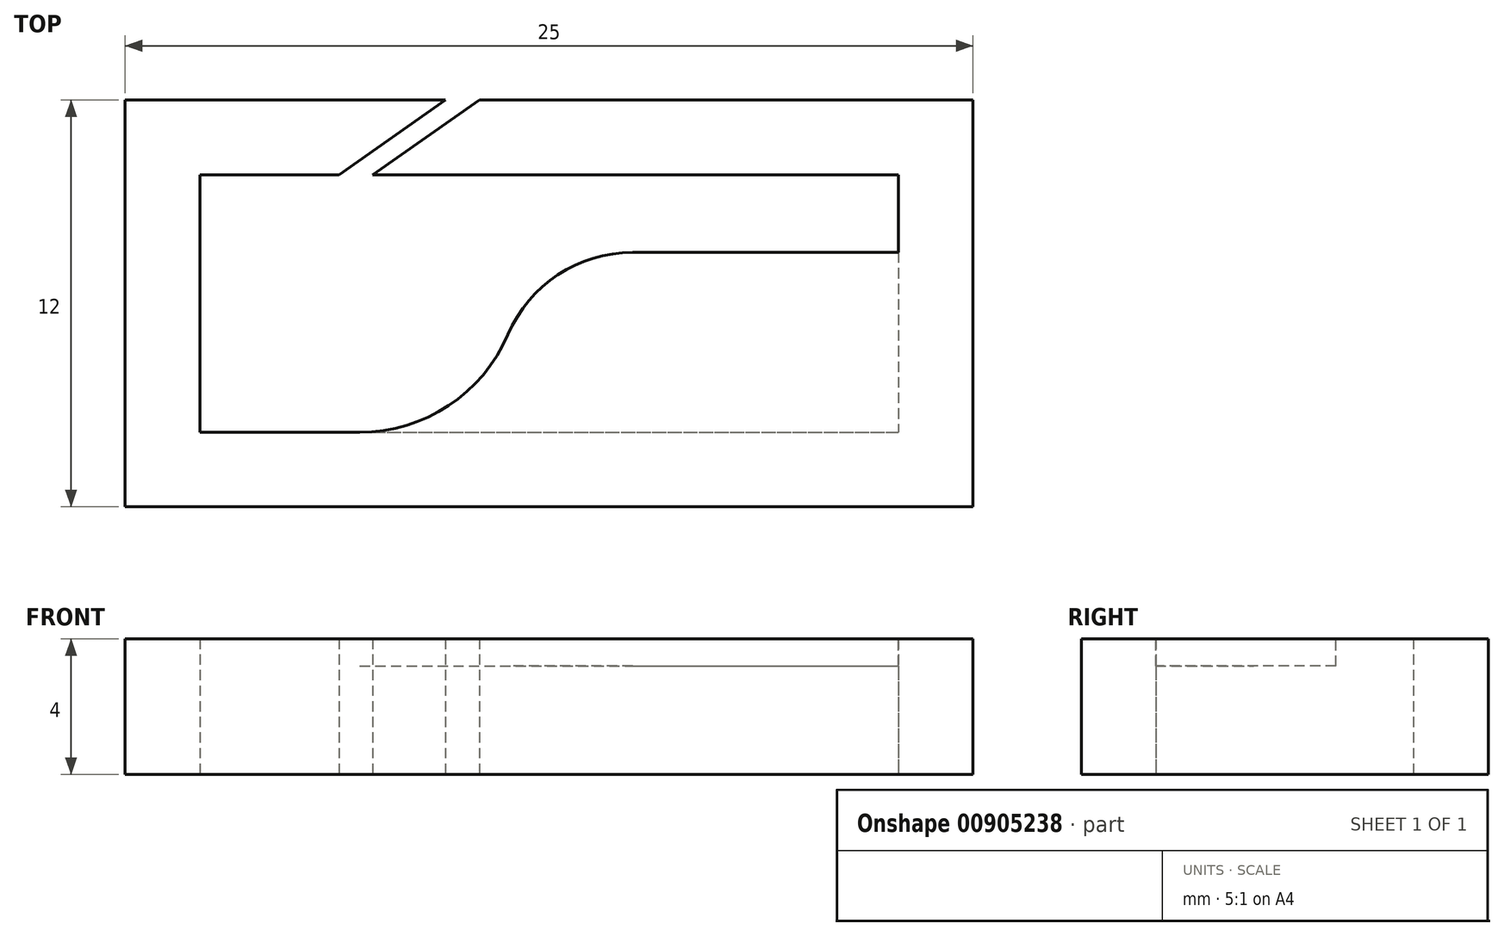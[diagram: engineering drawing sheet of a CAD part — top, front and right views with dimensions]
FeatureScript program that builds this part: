
annotation { "Feature Type Name" : "Feature", "Feature Type Description" : "" }
export const myFeature = defineFeature(function(context is Context, id is Id, definition is map)
    precondition{}
    {
        {
            var Q0;
            Q0=qCreatedBy(makeId("Top.planeOp"),FACE);
            var sketch = newSketch(context, id + "F0", { "sketchPlane" : qUnion([Q0])});
            skLineSegment(sketch, "E0.bottom", {"start": v(-18.57, -20.66) * mm, "end": v(-9.13, -20.66) * mm});
            skLineSegment(sketch, "E0.top", {"start": v(-18.57, -32.66) * mm, "end": v(6.43, -32.66) * mm});
            skLineSegment(sketch, "E0.left", {"start": v(-18.57, -20.66) * mm, "end": v(-18.57, -32.66) * mm});
            skLineSegment(sketch, "E0.right", {"start": v(6.43, -20.66) * mm, "end": v(6.43, -32.66) * mm});
            skLineSegment(sketch, "E1.0", {"start": v(-16.37, -22.86) * mm, "end": v(-16.37, -30.46) * mm});
            skLineSegment(sketch, "E1.1", {"start": v(-11.27, -22.86) * mm, "end": v(4.23, -22.86) * mm});
            skLineSegment(sketch, "E1.2", {"start": v(4.23, -22.86) * mm, "end": v(4.23, -30.46) * mm});
            skLineSegment(sketch, "E1.3", {"start": v(-16.37, -30.46) * mm, "end": v(4.23, -30.46) * mm});
            skLineSegment(sketch, "E2", {"start": v(-12.27, -22.86) * mm, "end": v(-9.13, -20.66) * mm});
            skLineSegment(sketch, "E3", {"start": v(-11.27, -22.86) * mm, "end": v(-8.13, -20.66) * mm});
            skLineSegment(sketch, "E4.trimOffspring", {"start": v(-8.13, -20.66) * mm, "end": v(6.43, -20.66) * mm});
            skLineSegment(sketch, "E5", {"start": v(-16.37, -22.86) * mm, "end": v(-12.27, -22.86) * mm});
            skSolve(sketch);
        }
        {
            var Q0;
            Q0=makeQuery(id+"F0.imprint","IMPRINT",FACE,{"disambiguationData":[TD([[makeQuery(id+"F0.imprint","IMPRINT",EDGE,{"derivedFrom":sQuery(id+"F0.wireOp",EDGE,"E0.bottom")}),-1.0]])]});
            extrude(context, id + "F1", {"entities" : qUnion([Q0]), "depth" : 4 * mm, "offsetDistance" : 25 * mm});
        }
        {
            var Q0;
            Q0=makeQuery(id+"F1.opExtrude","CAP_FACE",FACE,{"disambiguationData":[OSD([sQuery(id+"F0.wireOp",EDGE,"E0.bottom"),sQuery(id+"F0.wireOp",EDGE,"E0.top"),sQuery(id+"F0.wireOp",EDGE,"E0.left"),sQuery(id+"F0.wireOp",EDGE,"E0.right"),sQuery(id+"F0.wireOp",EDGE,"E1.0"),sQuery(id+"F0.wireOp",EDGE,"E1.1"),sQuery(id+"F0.wireOp",EDGE,"E1.2"),sQuery(id+"F0.wireOp",EDGE,"E1.3"),sQuery(id+"F0.wireOp",EDGE,"E2"),sQuery(id+"F0.wireOp",EDGE,"E3"),sQuery(id+"F0.wireOp",EDGE,"E4.trimOffspring"),sQuery(id+"F0.wireOp",EDGE,"E5")])],"isStart":false});
            var sketch = newSketch(context, id + "F2", { "sketchPlane" : qUnion([Q0])});
            skLineSegment(sketch, "E6.bottom", {"start": v(-11.65, -31.16) * mm, "end": v(6.43, -31.16) * mm});
            skLineSegment(sketch, "E6.top", {"start": v(-3.6, -25.16) * mm, "end": v(6.43, -25.16) * mm});
            skLineSegment(sketch, "E6.right", {"start": v(6.43, -31.16) * mm, "end": v(6.43, -25.16) * mm});
            skArc(sketch, "E7", {"start": v(-11.65, -30.46) * mm, "mid": v(-9.04, -29.68) * mm, "end": v(-7.28, -27.58) * mm});
            skPoint(sketch, "E8.visualSharp", {"position": v(-6.93, -25.16) * mm});
            skArc(sketch, "E8.filletArc", {"start": v(-3.6, -25.16) * mm, "mid": v(-5.8, -25.82) * mm, "end": v(-7.28, -27.58) * mm});
            skLineSegment(sketch, "E9", {"start": v(-11.65, -30.46) * mm, "end": v(-11.65, -31.16) * mm});
            skSolve(sketch);
        }
        {
            var Q0;
            {var subQ0=makeQuery(id+"F1.opExtrude","CAP_EDGE",EDGE,{"disambiguationData":[OSD([sQuery(id+"F0.wireOp",EDGE,"E1.3")])],"isStart":false});Q0=makeQuery(id+"F2.imprint","IMPRINT",FACE,{"disambiguationData":[TD([[makeQuery(id+"F2.imprint","IMPRINT",EDGE,{"derivedFrom":subQ0}),1.0]])]});}
            extrude(context, id + "F3", {"entities" : qUnion([Q0]), "operationType" : NewBodyOperationType.ADD, "oppositeDirection" : true, "depth" : .8 * mm, "offsetDistance" : 25 * mm});
        }
    });
